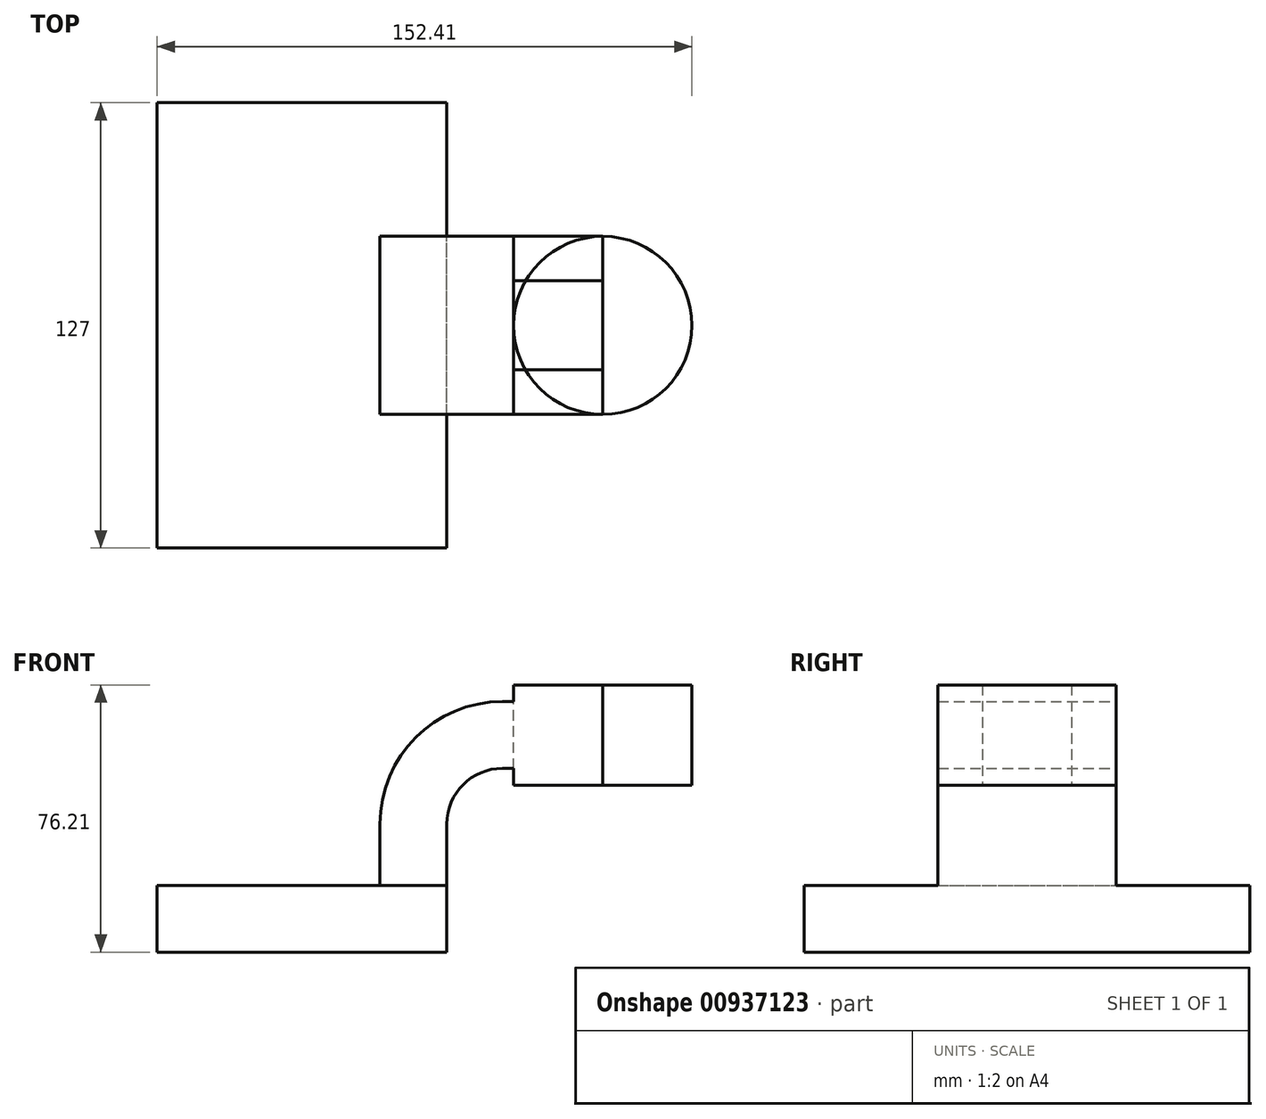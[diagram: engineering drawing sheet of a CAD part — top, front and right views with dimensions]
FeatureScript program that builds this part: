
annotation { "Feature Type Name" : "Feature", "Feature Type Description" : "" }
export const myFeature = defineFeature(function(context is Context, id is Id, definition is map)
    precondition{}
    {
        {
            var Q0;
            Q0=qCreatedBy(makeId("Front.planeOp"),FACE);
            var sketch = newSketch(context, id + "F0", { "sketchPlane" : qUnion([Q0])});
            skLineSegment(sketch, "E0.bottom", {"start": v(-41.28, -9.52) * mm, "end": v(41.28, -9.52) * mm});
            skLineSegment(sketch, "E0.top", {"start": v(-41.28, 9.53) * mm, "end": v(41.28, 9.53) * mm});
            skLineSegment(sketch, "E0.left", {"start": v(-41.28, -9.52) * mm, "end": v(-41.28, 9.53) * mm});
            skLineSegment(sketch, "E0.right", {"start": v(41.28, -9.53) * mm, "end": v(41.28, 9.52) * mm});
            skPoint(sketch, "E0.middle", {"position": v(0, 0) * mm});
            skLineSegment(sketch, "E1.bottom", {"start": v(111.12, 38.1) * mm, "end": v(60.32, 38.1) * mm});
            skLineSegment(sketch, "E1.top", {"start": v(111.12, 66.67) * mm, "end": v(60.32, 66.67) * mm});
            skLineSegment(sketch, "E1.left", {"start": v(111.12, 38.1) * mm, "end": v(111.12, 66.67) * mm});
            skLineSegment(sketch, "E1.right", {"start": v(60.32, 38.1) * mm, "end": v(60.32, 66.67) * mm});
            skPoint(sketch, "E1.middle", {"position": v(85.72, 52.39) * mm});
            skLineSegment(sketch, "E2", {"start": v(41.28, 9.52) * mm, "end": v(41.28, 27) * mm});
            skArc(sketch, "E3", {"start": v(41.27, 27) * mm, "mid": v(45.92, 38.23) * mm, "end": v(57.15, 42.88) * mm});
            skLineSegment(sketch, "E4", {"start": v(57.15, 42.88) * mm, "end": v(60.32, 42.88) * mm});
            skLineSegment(sketch, "E5.0", {"start": v(57.15, 61.93) * mm, "end": v(60.32, 61.93) * mm});
            skArc(sketch, "E5.1", {"start": v(22.23, 27) * mm, "mid": v(32.45, 51.7) * mm, "end": v(57.15, 61.93) * mm});
            skLineSegment(sketch, "E5.2", {"start": v(22.22, 9.52) * mm, "end": v(22.22, 27) * mm});
            skPoint(sketch, "E6.end.orphan", {"position": v(85.72, 66.67) * mm});
            skLineSegment(sketch, "E7", {"start": v(85.72, 61.93) * mm, "end": v(85.72, 42.88) * mm});
            skFitSpline(sketch, "E8", {"points": [v(-41.28, 9.53) * mm, v(57.15, 61.93) * mm], "startDerivative": vector(31.3, 82.71) * mm, "endDerivative": vector(170.27, -5.23) * mm});
            skLineSegment(sketch, "E9", {"start": v(85.72, 66.67) * mm, "end": v(85.72, 38.1) * mm});
            skSolve(sketch);
        }
        {
            var Q0;
            Q0=makeQuery(id+"F0.imprint","IMPRINT",FACE,{"disambiguationData":[TD([[makeQuery(id+"F0.imprint","IMPRINT",EDGE,{"derivedFrom":sQuery(id+"F0.wireOp",EDGE,"E0.bottom")}),1.0]])]});
            extrude(context, id + "F1", {"entities" : qUnion([Q0]), "endBound" : BoundingType.SYMMETRIC, "depth" : 127 * mm, "offsetDistance" : 25.4 * mm});
        }
        {
            var Q0;
            {var subQ5=sQuery(id+"F0.wireOp",EDGE,"E7");Q0=makeQuery(id+"F0.imprint","IMPRINT",FACE,{"disambiguationData":[TD([[makeQuery(id+"F0.imprint","IMPRINT",EDGE,{"derivedFrom":subQ5}),-1.0]])]});}
            var Q1;
            {var subQ0=sQuery(id+"F0.wireOp",EDGE,"E2");Q1=makeQuery(id+"F0.imprint","IMPRINT",FACE,{"disambiguationData":[TD([[makeQuery(id+"F0.imprint","IMPRINT",EDGE,{"derivedFrom":subQ0}),1.0]])]});}
            extrude(context, id + "F2", {"entities" : qUnion([Q0, Q1]), "operationType" : NewBodyOperationType.ADD, "endBound" : BoundingType.SYMMETRIC, "depth" : 50.8 * mm, "offsetDistance" : 25.4 * mm});
        }
        {
            var Q0;
            Q0=makeQuery(id+"F0.imprint","IMPRINT",FACE,{"disambiguationData":[TD([[makeQuery(id+"F0.imprint","IMPRINT",EDGE,{"derivedFrom":sQuery(id+"F0.wireOp",EDGE,"E5.1")}),1.0]])]});
            extrude(context, id + "F3", {"entities" : qUnion([Q0]), "operationType" : NewBodyOperationType.ADD, "endBound" : BoundingType.SYMMETRIC, "depth" : 15.88 * mm, "offsetDistance" : 25.4 * mm});
        }
        {
            var Q0;
            {var subQ1=sQuery(id+"F0.wireOp",EDGE,"E1.bottom");Q0=makeQuery(id+"F0.imprint","IMPRINT",FACE,{"disambiguationData":[TD([[makeQuery(id+"F0.imprint","IMPRINT",EDGE,{"derivedFrom":subQ1}),-1.0]])]});}
            var Q1;
            Q1=sQuery(id+"F0.wireOp",EDGE,"E7");
            revolve(context, id + "F4", {"surfaceOperationType" : NewSurfaceOperationType.NEW, "entities" : qUnion([Q0]), "axis" : qUnion([Q1]), "revolveType" : RevolveType.FULL});
        }
        {
            var Q0;
            {var subQ0=sQuery(id+"F0.wireOp",EDGE,"E4");var subQ1=sQuery(id+"F0.wireOp",EDGE,"E1.right");var subQ2=makeQuery(id+"F0.imprint","INTERSECT",VERTEX,{"derivedFrom":[subQ1,subQ0]});Q0=makeQuery(id+"F0.imprint","IMPRINT",FACE,{"disambiguationData":[TD([[makeQuery(id+"F0.imprint","IMPRINT",EDGE,{"disambiguationData":[TD([[subQ2,-1.0]])],"derivedFrom":subQ1}),-1.0]])]});}
            extrude(context, id + "F5", {"entities" : qUnion([Q0]), "endBound" : BoundingType.SYMMETRIC, "depth" : 25.4 * mm, "offsetDistance" : 25.4 * mm});
        }
    });
